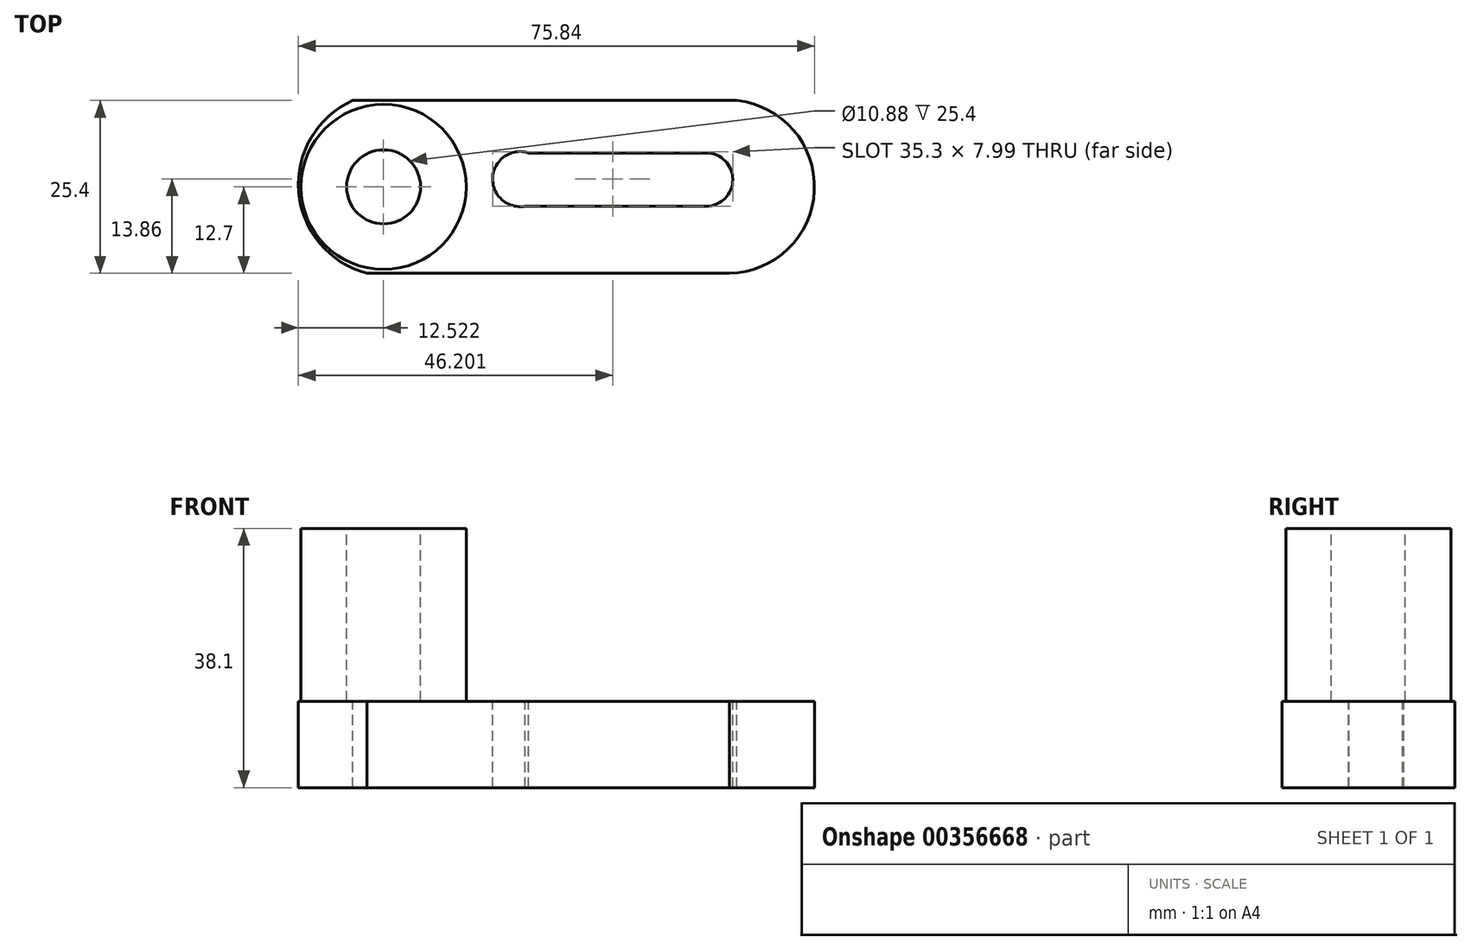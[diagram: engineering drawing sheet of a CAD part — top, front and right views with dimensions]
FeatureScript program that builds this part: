
annotation { "Feature Type Name" : "Feature", "Feature Type Description" : "" }
export const myFeature = defineFeature(function(context is Context, id is Id, definition is map)
    precondition{}
    {
        {
            var Q0;
            Q0=qCreatedBy(makeId("Front.planeOp"),FACE);
            var sketch = newSketch(context, id + "F0", { "sketchPlane" : qUnion([Q0])});
            skLineSegment(sketch, "E0", {"start": v(-31.66, 24.36) * mm, "end": v(-6.26, 24.36) * mm});
            skLineSegment(sketch, "E1", {"start": v(-6.26, 24.36) * mm, "end": v(-6.26, -1.04) * mm});
            skLineSegment(sketch, "E2", {"start": v(-6.26, -1.04) * mm, "end": v(44.54, -1.04) * mm});
            skLineSegment(sketch, "E3", {"start": v(44.54, -1.04) * mm, "end": v(44.54, -13.74) * mm});
            skLineSegment(sketch, "E4", {"start": v(44.54, -13.74) * mm, "end": v(-31.66, -13.74) * mm});
            skLineSegment(sketch, "E5", {"start": v(-31.66, -13.74) * mm, "end": v(-31.66, 24.36) * mm});
            skSolve(sketch);
        }
        {
            var Q0;
            Q0=makeQuery(id+"F0.imprint","IMPRINT",FACE,{"disambiguationData":[TD([[makeQuery(id+"F0.imprint","IMPRINT",EDGE,{"derivedFrom":sQuery(id+"F0.wireOp",EDGE,"E0")}),-1.0]])]});
            extrude(context, id + "F1", {"entities" : qUnion([Q0]), "depth" : 25.4 * mm});
        }
        {
            var Q0;
            Q0=makeQuery(id+"F1.opExtrude","SWEPT_FACE",FACE,{"disambiguationData":[OSD([sQuery(id+"F0.wireOp",EDGE,"E2")])]});
            var sketch = newSketch(context, id + "F2", { "sketchPlane" : qUnion([Q0])});
            skArc(sketch, "E6", {"start": v(31.85, -25.4) * mm, "mid": v(44.34, -11.88) * mm, "end": v(30.28, 0) * mm});
            skSolve(sketch);
        }
        {
            var Q0;
            {var subQ1=sQuery(id+"F0.wireOp",EDGE,"E2");var subQ6=makeQuery(id+"F1.opExtrude","SWEPT_EDGE",EDGE,{"disambiguationData":[OSD([subQ1,sQuery(id+"F0.wireOp",EDGE,"E3")])]});Q0=makeQuery(id+"F2.imprint","IMPRINT",FACE,{"disambiguationData":[TD([[makeQuery(id+"F2.imprint","IMPRINT",EDGE,{"derivedFrom":subQ6}),1.0]])]});}
            extrude(context, id + "F3", {"entities" : qUnion([Q0]), "operationType" : NewBodyOperationType.REMOVE, "oppositeDirection" : true, "depth" : 25.4 * mm});
        }
        {
            var Q0;
            Q0=makeQuery(id+"F1.opExtrude","SWEPT_FACE",FACE,{"disambiguationData":[OSD([sQuery(id+"F0.wireOp",EDGE,"E0")])]});
            var sketch = newSketch(context, id + "F4", { "sketchPlane" : qUnion([Q0])});
            skCircle(sketch, "E7", {"center": v(-18.96, -12.7) * mm, "radius": 12.13 * mm});
            skPoint(sketch, "E7.centerSnap0", {"position": v(-6.26, -12.7) * mm});
            skPoint(sketch, "E7.centerSnap1", {"position": v(-18.96, -25.4) * mm});
            skCircle(sketch, "E8", {"center": v(-18.96, -12.7) * mm, "radius": 5.44 * mm});
            skSolve(sketch);
        }
        {
            var Q0;
            Q0=makeQuery(id+"F4.imprint","IMPRINT",FACE,{"disambiguationData":[TD([[makeQuery(id+"F4.imprint","IMPRINT",EDGE,{"derivedFrom":sQuery(id+"F4.wireOp",EDGE,"E7")}),-1.0]])]});
            var Q1;
            Q1=makeQuery(id+"F4.imprint","IMPRINT",FACE,{"disambiguationData":[TD([[makeQuery(id+"F4.imprint","IMPRINT",EDGE,{"derivedFrom":sQuery(id+"F4.wireOp",EDGE,"E8")}),1.0]])]});
            extrude(context, id + "F5", {"entities" : qUnion([Q0, Q1]), "operationType" : NewBodyOperationType.REMOVE, "oppositeDirection" : true, "depth" : 25.4 * mm});
        }
        {
            var Q0;
            Q0=makeQuery(id+"F5.boolean.opBoolean","MERGE",FACE,{"derivedFrom":[makeQuery(id+"F1.opExtrude","SWEPT_FACE",FACE,{"disambiguationData":[OSD([sQuery(id+"F0.wireOp",EDGE,"E2")])]}),makeQuery(id+"F5.opExtrude","CAP_FACE",FACE,{"disambiguationData":[OSD([sQuery(id+"F0.wireOp",EDGE,"E0"),sQuery(id+"F0.wireOp",EDGE,"E1"),sQuery(id+"F0.wireOp",EDGE,"E5"),sQuery(id+"F4.wireOp",EDGE,"E7")])],"isStart":false})]});
            var sketch = newSketch(context, id + "F6", { "sketchPlane" : qUnion([Q0])});
            skLineSegment(sketch, "E9", {"start": v(-31.66, 0) * mm, "end": v(-23.5, 0) * mm});
            skLineSegment(sketch, "E10", {"start": v(-31.66, 0) * mm, "end": v(-31.66, -25.4) * mm});
            skLineSegment(sketch, "E11", {"start": v(-31.66, -25.4) * mm, "end": v(-21.4, -25.4) * mm});
            skArc(sketch, "E12", {"start": v(-23.5, 0) * mm, "mid": v(-31.43, -13.44) * mm, "end": v(-21.4, -25.4) * mm});
            skSolve(sketch);
        }
        {
            var Q0;
            Q0=makeQuery(id+"F6.imprint","IMPRINT",FACE,{"disambiguationData":[TD([[makeQuery(id+"F6.imprint","IMPRINT",EDGE,{"derivedFrom":sQuery(id+"F6.wireOp",EDGE,"E9")}),-1.0]])]});
            extrude(context, id + "F7", {"entities" : qUnion([Q0]), "operationType" : NewBodyOperationType.REMOVE, "oppositeDirection" : true, "depth" : 25.4 * mm});
        }
        {
            var Q0;
            Q0=makeQuery(id+"F5.boolean.opBoolean","MERGE",FACE,{"derivedFrom":[makeQuery(id+"F1.opExtrude","SWEPT_FACE",FACE,{"disambiguationData":[OSD([sQuery(id+"F0.wireOp",EDGE,"E2")])]}),makeQuery(id+"F5.opExtrude","CAP_FACE",FACE,{"disambiguationData":[OSD([sQuery(id+"F0.wireOp",EDGE,"E0"),sQuery(id+"F0.wireOp",EDGE,"E1"),sQuery(id+"F0.wireOp",EDGE,"E5"),sQuery(id+"F4.wireOp",EDGE,"E7")])],"isStart":false})]});
            var sketch = newSketch(context, id + "F8", { "sketchPlane" : qUnion([Q0])});
            skLineSegment(sketch, "E13", {"start": v(2.35, -7.7) * mm, "end": v(28.45, -7.7) * mm});
            skLineSegment(sketch, "E14", {"start": v(28.45, -15.53) * mm, "end": v(1.83, -15.53) * mm});
            skArc(sketch, "E15", {"start": v(28.45, -15.53) * mm, "mid": v(32.37, -11.62) * mm, "end": v(28.45, -7.7) * mm});
            skArc(sketch, "E16", {"start": v(2.35, -7.7) * mm, "mid": v(-2.93, -11.28) * mm, "end": v(1.83, -15.53) * mm});
            skSolve(sketch);
        }
        {
            var Q0;
            Q0=makeQuery(id+"F8.imprint","IMPRINT",FACE,{"disambiguationData":[TD([[makeQuery(id+"F8.imprint","IMPRINT",EDGE,{"derivedFrom":sQuery(id+"F8.wireOp",EDGE,"E13")}),-1.0]])]});
            extrude(context, id + "F9", {"entities" : qUnion([Q0]), "operationType" : NewBodyOperationType.REMOVE, "oppositeDirection" : true, "depth" : 25.4 * mm});
        }
    });
